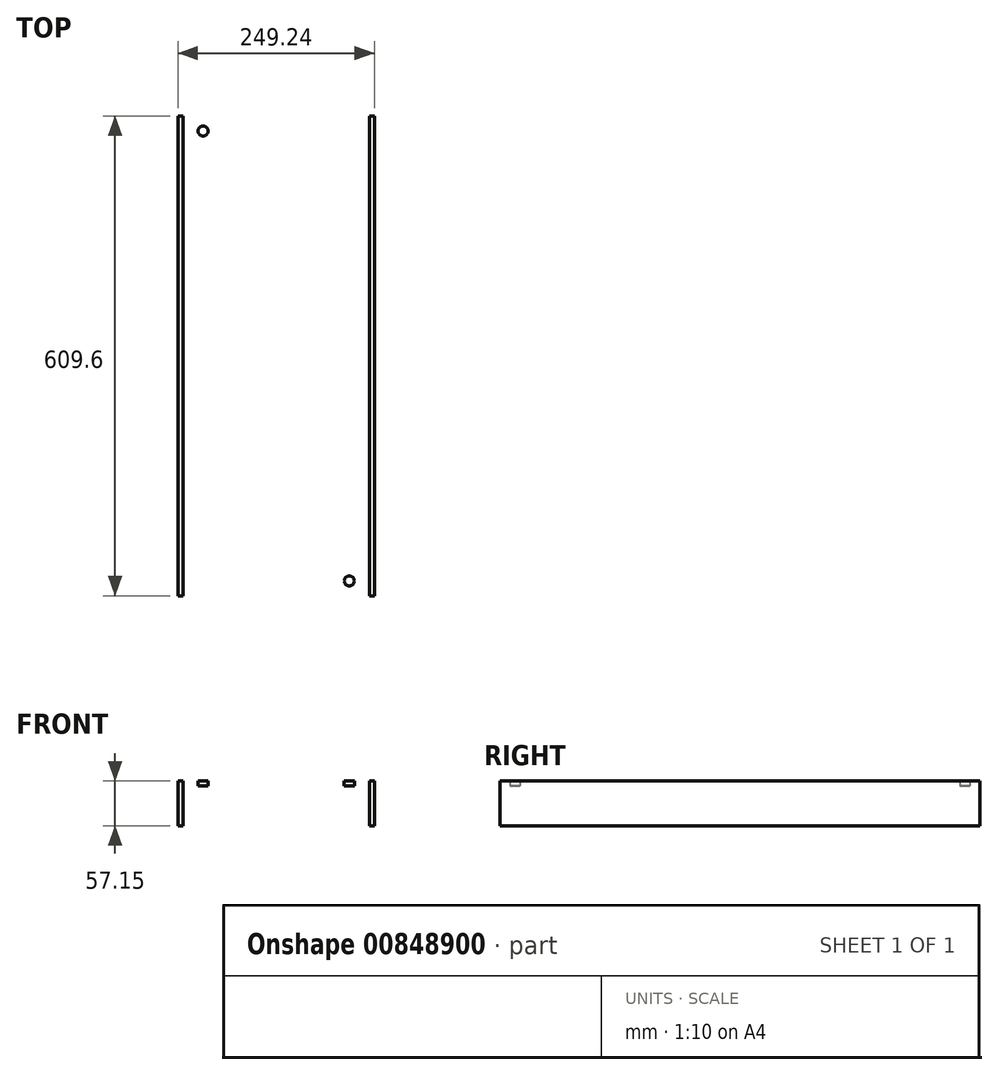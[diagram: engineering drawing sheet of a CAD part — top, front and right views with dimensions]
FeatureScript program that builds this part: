
annotation { "Feature Type Name" : "Feature", "Feature Type Description" : "" }
export const myFeature = defineFeature(function(context is Context, id is Id, definition is map)
    precondition{}
    {
        {
            var Q0;
            Q0=qCreatedBy(makeId("Top.planeOp"),FACE);
            var sketch = newSketch(context, id + "F0", { "sketchPlane" : qUnion([Q0])});
            skLineSegment(sketch, "E0.bottom", {"start": v(-124.62, -304.8) * mm, "end": v(124.62, -304.8) * mm});
            skLineSegment(sketch, "E0.top", {"start": v(-124.62, 304.8) * mm, "end": v(124.62, 304.8) * mm});
            skLineSegment(sketch, "E0.left", {"start": v(-124.62, -304.8) * mm, "end": v(-124.62, 304.8) * mm});
            skLineSegment(sketch, "E0.right", {"start": v(124.62, -304.8) * mm, "end": v(124.62, 304.8) * mm});
            skPoint(sketch, "E0.middle", {"position": v(0, 0) * mm});
            skLineSegment(sketch, "E1", {"start": v(0, 304.8) * mm, "end": v(0, 196.85) * mm});
            skLineSegment(sketch, "E2", {"start": v(0, 196.85) * mm, "end": v(0, 120.65) * mm});
            skLineSegment(sketch, "E3", {"start": v(-57.15, 120.65) * mm, "end": v(57.15, 120.65) * mm});
            skLineSegment(sketch, "E4", {"start": v(-57.15, 196.85) * mm, "end": v(57.15, 196.85) * mm});
            skCircle(sketch, "E5", {"center": v(-57.15, 196.85) * mm, "radius": 7.14 * mm});
            skCircle(sketch, "E6.MirrorC", {"center": v(57.15, 196.85) * mm, "radius": 7.14 * mm});
            skLineSegment(sketch, "E7", {"start": v(0, 158.75) * mm, "end": v(22.39, 158.75) * mm});
            skCircle(sketch, "E8.MirrorC", {"center": v(57.15, 120.65) * mm, "radius": 7.14 * mm});
            skCircle(sketch, "E9.MirrorC", {"center": v(-57.15, 120.65) * mm, "radius": 7.14 * mm});
            skLineSegment(sketch, "E10", {"start": v(0, 120.65) * mm, "end": v(0, -123.82) * mm});
            skLineSegment(sketch, "E11", {"start": v(-69.85, -123.82) * mm, "end": v(69.85, -123.82) * mm});
            skLineSegment(sketch, "E12", {"start": v(0, -123.82) * mm, "end": v(0, -225.42) * mm});
            skLineSegment(sketch, "E13", {"start": v(-69.85, -225.43) * mm, "end": v(69.85, -225.43) * mm});
            skCircle(sketch, "E14", {"center": v(-69.85, -123.82) * mm, "radius": 5.56 * mm});
            skCircle(sketch, "E15.MirrorC", {"center": v(69.85, -123.82) * mm, "radius": 5.56 * mm});
            skLineSegment(sketch, "E16", {"start": v(0, -174.62) * mm, "end": v(-33.54, -174.62) * mm});
            skCircle(sketch, "E17.MirrorC", {"center": v(-69.85, -225.42) * mm, "radius": 5.56 * mm});
            skCircle(sketch, "E18.MirrorC", {"center": v(69.85, -225.42) * mm, "radius": 5.56 * mm});
            skSolve(sketch);
        }
        {
            var Q0;
            Q0 = qSketchRegion(id + "F0", true);
            extrude(context, id + "F1", {"entities" : qUnion([Q0]), "depth" : 6.35 * mm, "offsetDistance" : 25.4 * mm});
        }
        {
            var Q0;
            Q0=makeQuery(id+"F1.opExtrude","CAP_FACE",FACE,{"disambiguationData":[OSD([sQuery(id+"F0.wireOp",EDGE,"E0.bottom"),sQuery(id+"F0.wireOp",EDGE,"E0.top"),sQuery(id+"F0.wireOp",EDGE,"E0.left"),sQuery(id+"F0.wireOp",EDGE,"E0.right")])],"isStart":true});
            var sketch = newSketch(context, id + "F2", { "sketchPlane" : qUnion([Q0])});
            skLineSegment(sketch, "E19.bottom", {"start": v(-124.62, 304.8) * mm, "end": v(-118.27, 304.8) * mm});
            skLineSegment(sketch, "E19.top", {"start": v(-124.62, -304.8) * mm, "end": v(-118.27, -304.8) * mm});
            skLineSegment(sketch, "E19.left", {"start": v(-124.62, 304.8) * mm, "end": v(-124.62, -304.8) * mm});
            skLineSegment(sketch, "E19.right", {"start": v(-118.27, 304.8) * mm, "end": v(-118.27, -304.8) * mm});
            skLineSegment(sketch, "E20", {"start": v(0, 304.8) * mm, "end": v(0, 268.67) * mm});
            skLineSegment(sketch, "E21.MirrorCS", {"start": v(118.27, 304.8) * mm, "end": v(118.27, -304.8) * mm});
            skLineSegment(sketch, "E22.MirrorCS", {"start": v(124.62, 304.8) * mm, "end": v(124.62, -304.8) * mm});
            skLineSegment(sketch, "E23.MirrorCS", {"start": v(124.62, 304.8) * mm, "end": v(118.27, 304.8) * mm});
            skLineSegment(sketch, "E24.MirrorCS", {"start": v(124.62, -304.8) * mm, "end": v(118.27, -304.8) * mm});
            skSolve(sketch);
        }
        {
            var Q0;
            Q0 = qSketchRegion(id + "F2", true);
            extrude(context, id + "F3", {"entities" : qUnion([Q0]), "operationType" : NewBodyOperationType.ADD, "depth" : 50.8 * mm, "offsetDistance" : 25.4 * mm});
        }
        {
            var Q0;
            Q0=makeQuery(id+"F1.opExtrude","CAP_FACE",FACE,{"disambiguationData":[OSD([sQuery(id+"F0.wireOp",EDGE,"E0.bottom"),sQuery(id+"F0.wireOp",EDGE,"E0.top"),sQuery(id+"F0.wireOp",EDGE,"E0.left"),sQuery(id+"F0.wireOp",EDGE,"E0.right"),sQuery(id+"F0.wireOp",EDGE,"E5"),sQuery(id+"F0.wireOp",EDGE,"E6.MirrorC"),sQuery(id+"F0.wireOp",EDGE,"E8.MirrorC"),sQuery(id+"F0.wireOp",EDGE,"E9.MirrorC"),sQuery(id+"F0.wireOp",EDGE,"E14"),sQuery(id+"F0.wireOp",EDGE,"E15.MirrorC"),sQuery(id+"F0.wireOp",EDGE,"E17.MirrorC"),sQuery(id+"F0.wireOp",EDGE,"E18.MirrorC")])],"isStart":false});
            var sketch = newSketch(context, id + "F4", { "sketchPlane" : qUnion([Q0])});
            skLineSegment(sketch, "E25", {"start": v(-69.85, -123.82) * mm, "end": v(-69.85, -225.42) * mm});
            skLineSegment(sketch, "E26.bottom", {"start": v(-44.45, -257.17) * mm, "end": v(-95.25, -257.17) * mm});
            skLineSegment(sketch, "E26.top", {"start": v(-44.45, -92.07) * mm, "end": v(-95.25, -92.07) * mm});
            skLineSegment(sketch, "E26.left", {"start": v(-44.45, -257.17) * mm, "end": v(-44.45, -92.07) * mm});
            skLineSegment(sketch, "E26.right", {"start": v(-95.25, -257.17) * mm, "end": v(-95.25, -92.07) * mm});
            skPoint(sketch, "E26.middle", {"position": v(-69.85, -174.62) * mm});
            skLineSegment(sketch, "E27", {"start": v(0, 0) * mm, "end": v(0, -82.27) * mm});
            skLineSegment(sketch, "E28.MirrorCS", {"start": v(44.45, -92.07) * mm, "end": v(95.25, -92.07) * mm});
            skLineSegment(sketch, "E29.MirrorCS", {"start": v(44.45, -257.17) * mm, "end": v(44.45, -92.07) * mm});
            skLineSegment(sketch, "E30.MirrorCS", {"start": v(95.25, -257.17) * mm, "end": v(95.25, -92.07) * mm});
            skLineSegment(sketch, "E31.MirrorCS", {"start": v(44.45, -257.17) * mm, "end": v(95.25, -257.17) * mm});
            skSolve(sketch);
        }
        {
            var Q0;
            Q0 = qSketchRegion(id + "F4", true);
            extrude(context, id + "F5", {"entities" : qUnion([Q0]), "operationType" : NewBodyOperationType.ADD, "depth" : 19.05 * mm, "offsetDistance" : 25.4 * mm});
        }
        {
            var Q0;
            Q0=makeQuery(id+"F5.boolean.opBoolean","SPLIT",FACE,{"disambiguationData":[TD([makeQuery(id+"F1.opExtrude","SWEPT_FACE",FACE,{"disambiguationData":[OSD([sQuery(id+"F0.wireOp",EDGE,"E14")])]})])],"derivedFrom":makeQuery(id+"F5.opExtrude","CAP_FACE",FACE,{"disambiguationData":[OSD([sQuery(id+"F4.wireOp",EDGE,"E26.bottom"),sQuery(id+"F4.wireOp",EDGE,"E26.top"),sQuery(id+"F4.wireOp",EDGE,"E26.left"),sQuery(id+"F4.wireOp",EDGE,"E26.right")])],"isStart":true})});
            var Q1;
            Q1=makeQuery(id+"F5.boolean.opBoolean","SPLIT",FACE,{"disambiguationData":[TD([makeQuery(id+"F1.opExtrude","SWEPT_FACE",FACE,{"disambiguationData":[OSD([sQuery(id+"F0.wireOp",EDGE,"E17.MirrorC")])]})])],"derivedFrom":makeQuery(id+"F5.opExtrude","CAP_FACE",FACE,{"disambiguationData":[OSD([sQuery(id+"F4.wireOp",EDGE,"E26.bottom"),sQuery(id+"F4.wireOp",EDGE,"E26.top"),sQuery(id+"F4.wireOp",EDGE,"E26.left"),sQuery(id+"F4.wireOp",EDGE,"E26.right")])],"isStart":true})});
            var Q2;
            Q2=makeQuery(id+"F5.boolean.opBoolean","SPLIT",FACE,{"disambiguationData":[TD([makeQuery(id+"F1.opExtrude","SWEPT_FACE",FACE,{"disambiguationData":[OSD([sQuery(id+"F0.wireOp",EDGE,"E18.MirrorC")])]})])],"derivedFrom":makeQuery(id+"F5.opExtrude","CAP_FACE",FACE,{"disambiguationData":[OSD([sQuery(id+"F4.wireOp",EDGE,"E28.MirrorCS"),sQuery(id+"F4.wireOp",EDGE,"E29.MirrorCS"),sQuery(id+"F4.wireOp",EDGE,"E30.MirrorCS"),sQuery(id+"F4.wireOp",EDGE,"E31.MirrorCS")])],"isStart":true})});
            var Q3;
            Q3=makeQuery(id+"F5.boolean.opBoolean","SPLIT",FACE,{"disambiguationData":[TD([makeQuery(id+"F1.opExtrude","SWEPT_FACE",FACE,{"disambiguationData":[OSD([sQuery(id+"F0.wireOp",EDGE,"E15.MirrorC")])]})])],"derivedFrom":makeQuery(id+"F5.opExtrude","CAP_FACE",FACE,{"disambiguationData":[OSD([sQuery(id+"F4.wireOp",EDGE,"E28.MirrorCS"),sQuery(id+"F4.wireOp",EDGE,"E29.MirrorCS"),sQuery(id+"F4.wireOp",EDGE,"E30.MirrorCS"),sQuery(id+"F4.wireOp",EDGE,"E31.MirrorCS")])],"isStart":true})});
            extrude(context, id + "F6", {"entities" : qUnion([Q0, Q1, Q2, Q3]), "operationType" : NewBodyOperationType.REMOVE, "oppositeDirection" : true, "depth" : 25.4 * mm, "offsetDistance" : 25.4 * mm});
        }
        {
            var Q0;
            Q0=makeQuery(id+"F1.opExtrude","CAP_FACE",FACE,{"disambiguationData":[OSD([sQuery(id+"F0.wireOp",EDGE,"E0.bottom"),sQuery(id+"F0.wireOp",EDGE,"E0.top"),sQuery(id+"F0.wireOp",EDGE,"E0.left"),sQuery(id+"F0.wireOp",EDGE,"E0.right"),sQuery(id+"F0.wireOp",EDGE,"E5"),sQuery(id+"F0.wireOp",EDGE,"E6.MirrorC"),sQuery(id+"F0.wireOp",EDGE,"E8.MirrorC"),sQuery(id+"F0.wireOp",EDGE,"E9.MirrorC"),sQuery(id+"F0.wireOp",EDGE,"E14"),sQuery(id+"F0.wireOp",EDGE,"E15.MirrorC"),sQuery(id+"F0.wireOp",EDGE,"E17.MirrorC"),sQuery(id+"F0.wireOp",EDGE,"E18.MirrorC")])],"isStart":true});
            var sketch = newSketch(context, id + "F7", { "sketchPlane" : qUnion([Q0])});
            skCircle(sketch, "E32", {"center": v(-92.87, 285.75) * mm, "radius": 6.35 * mm});
            skCircle(sketch, "E33.MirrorC", {"center": v(92.87, 285.75) * mm, "radius": 6.35 * mm});
            skCircle(sketch, "E34.MirrorC", {"center": v(92.87, -285.75) * mm, "radius": 6.35 * mm});
            skCircle(sketch, "E35.MirrorC", {"center": v(-92.87, -285.75) * mm, "radius": 6.35 * mm});
            skSolve(sketch);
        }
        {
            var Q0;
            Q0=makeQuery(id+"F7.imprint","IMPRINT",FACE,{"disambiguationData":[TD([[makeQuery(id+"F7.imprint","IMPRINT",EDGE,{"derivedFrom":sQuery(id+"F7.wireOp",EDGE,"E32")}),1.0]])]});
            var Q1;
            Q1=makeQuery(id+"F7.imprint","IMPRINT",FACE,{"disambiguationData":[TD([[makeQuery(id+"F7.imprint","IMPRINT",EDGE,{"derivedFrom":sQuery(id+"F7.wireOp",EDGE,"E33.MirrorC")}),-1.0]])]});
            var Q2;
            Q2=makeQuery(id+"F7.imprint","IMPRINT",FACE,{"disambiguationData":[TD([[makeQuery(id+"F7.imprint","IMPRINT",EDGE,{"derivedFrom":sQuery(id+"F7.wireOp",EDGE,"E34.MirrorC")}),1.0]])]});
            var Q3;
            Q3=makeQuery(id+"F7.imprint","IMPRINT",FACE,{"disambiguationData":[TD([[makeQuery(id+"F7.imprint","IMPRINT",EDGE,{"derivedFrom":sQuery(id+"F7.wireOp",EDGE,"E35.MirrorC")}),-1.0]])]});
            extrude(context, id + "F8", {"entities" : qUnion([Q0, Q1, Q2, Q3]), "operationType" : NewBodyOperationType.REMOVE, "oppositeDirection" : true, "depth" : 25.4 * mm, "offsetDistance" : 25.4 * mm});
        }
    });
